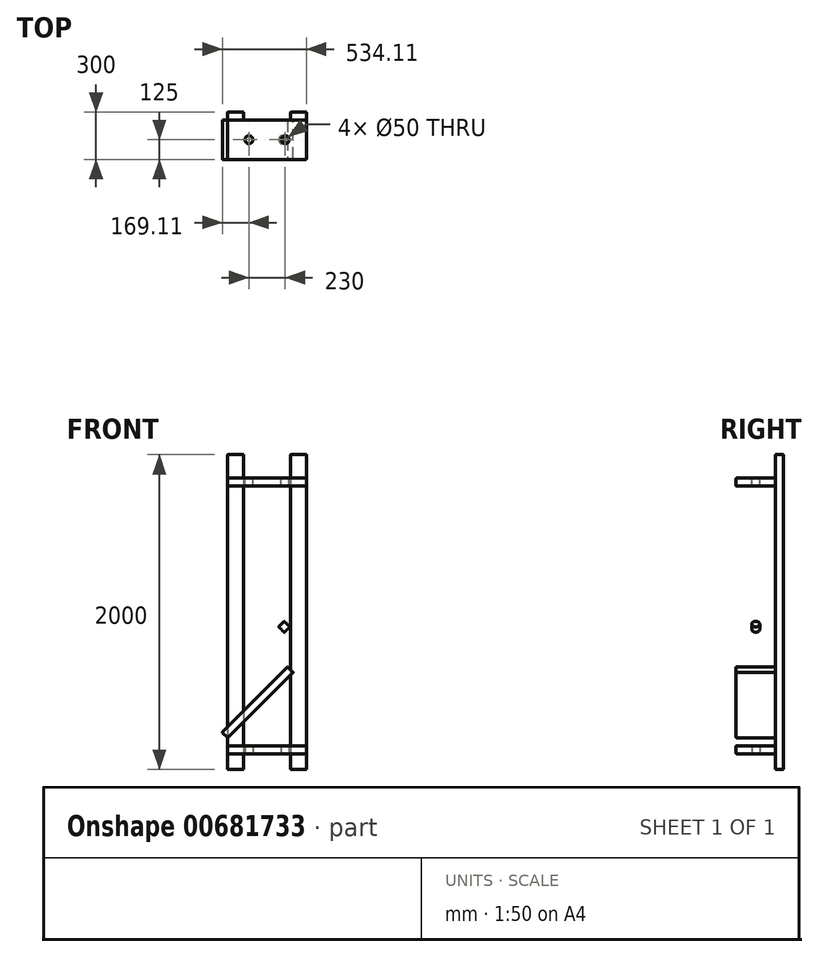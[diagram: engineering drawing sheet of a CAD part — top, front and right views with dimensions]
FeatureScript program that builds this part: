
annotation { "Feature Type Name" : "Feature", "Feature Type Description" : "" }
export const myFeature = defineFeature(function(context is Context, id is Id, definition is map)
    precondition{}
    {
        {
            var Q0;
            Q0=qCreatedBy(makeId("Top.planeOp"),FACE);
            var sketch = newSketch(context, id + "F0", { "sketchPlane" : qUnion([Q0])});
            skLineSegment(sketch, "E0", {"start": v(0, -23.34) * mm, "end": v(0, 25.87) * mm, "construction": true});
            skLineSegment(sketch, "E1.bottom", {"start": v(-250, 50) * mm, "end": v(-150, 50) * mm});
            skLineSegment(sketch, "E1.top", {"start": v(-250, 0) * mm, "end": v(-150, 0) * mm});
            skLineSegment(sketch, "E1.left", {"start": v(-250, 50) * mm, "end": v(-250, 0) * mm});
            skLineSegment(sketch, "E1.right", {"start": v(-150, 50) * mm, "end": v(-150, 0) * mm});
            skLineSegment(sketch, "E2.MirrorCS", {"start": v(150, 50) * mm, "end": v(150, 0) * mm});
            skLineSegment(sketch, "E3.MirrorCS", {"start": v(250, 50) * mm, "end": v(250, 0) * mm});
            skLineSegment(sketch, "E4.MirrorCS", {"start": v(250, 0) * mm, "end": v(150, 0) * mm});
            skLineSegment(sketch, "E5.MirrorCS", {"start": v(250, 50) * mm, "end": v(150, 50) * mm});
            skSolve(sketch);
        }
        {
            var Q0;
            Q0 = qSketchRegion(id + "F0", true);
            extrude(context, id + "F1", {"entities" : qUnion([Q0]), "depth" : 2000 * mm, "offsetDistance" : 25 * mm});
        }
        {
            var Q0;
            Q0=makeQuery(id+"F1.opExtrude","SWEPT_FACE",FACE,{"disambiguationData":[OSD([sQuery(id+"F0.wireOp",EDGE,"E1.top")])]});
            var sketch = newSketch(context, id + "F2", { "sketchPlane" : qUnion([Q0])});
            skLineSegment(sketch, "E6.bottom", {"start": v(-250, 1850) * mm, "end": v(250, 1850) * mm});
            skLineSegment(sketch, "E6.top", {"start": v(-250, 1800) * mm, "end": v(250, 1800) * mm});
            skLineSegment(sketch, "E6.left", {"start": v(-250, 1850) * mm, "end": v(-250, 1800) * mm});
            skLineSegment(sketch, "E6.right", {"start": v(250, 1850) * mm, "end": v(250, 1800) * mm});
            skLineSegment(sketch, "E7.bottom", {"start": v(-250, 150) * mm, "end": v(250, 150) * mm});
            skLineSegment(sketch, "E7.top", {"start": v(-250, 100) * mm, "end": v(250, 100) * mm});
            skLineSegment(sketch, "E7.left", {"start": v(-250, 150) * mm, "end": v(-250, 100) * mm});
            skLineSegment(sketch, "E7.right", {"start": v(250, 150) * mm, "end": v(250, 100) * mm});
            skLineSegment(sketch, "E8", {"start": v(300, 750) * mm, "end": v(-250, 1300) * mm});
            skLineSegment(sketch, "E9.MirrorCS", {"start": v(300, 750) * mm, "end": v(-250, 200) * mm});
            skLineSegment(sketch, "E10", {"start": v(-250, 1300) * mm, "end": v(-285.36, 1264.64) * mm});
            skLineSegment(sketch, "E11", {"start": v(-250, 200) * mm, "end": v(-285.36, 235.36) * mm});
            skLineSegment(sketch, "E12", {"start": v(-285.36, 1264.64) * mm, "end": v(229.29, 750) * mm});
            skLineSegment(sketch, "E13", {"start": v(229.29, 750) * mm, "end": v(-285.36, 235.36) * mm});
            skSolve(sketch);
        }
        {
            var Q0;
            Q0 = qSketchRegion(id + "F2", true);
            extrude(context, id + "F3", {"entities" : qUnion([Q0]), "depth" : 250 * mm, "offsetDistance" : 25 * mm});
        }
        {
            var Q0;
            Q0=makeQuery(id+"F3.opExtrude","SWEPT_FACE",FACE,{"disambiguationData":[OSD([sQuery(id+"F2.wireOp",EDGE,"E6.bottom")])]});
            var sketch = newSketch(context, id + "F4", { "sketchPlane" : qUnion([Q0])});
            skCircle(sketch, "E14", {"center": v(-115, -125) * mm, "radius": 25 * mm});
            skLineSegment(sketch, "E15", {"start": v(0, 0) * mm, "end": v(0, -300.8) * mm, "construction": true});
            skCircle(sketch, "E16.MirrorC", {"center": v(115, -125) * mm, "radius": 25 * mm});
            skSolve(sketch);
        }
        {
            var Q0;
            Q0 = qSketchRegion(id + "F4", true);
            extrude(context, id + "F5", {"entities" : qUnion([Q0]), "operationType" : NewBodyOperationType.REMOVE, "oppositeDirection" : true, "depth" : 128 * mm, "offsetDistance" : 25 * mm});
        }
        {
            var Q0;
            Q0=makeQuery(id+"F3.opExtrude","SWEPT_FACE",FACE,{"disambiguationData":[OSD([sQuery(id+"F2.wireOp",EDGE,"E7.top")])]});
            var sketch = newSketch(context, id + "F6", { "sketchPlane" : qUnion([Q0])});
            skCircle(sketch, "E17", {"center": v(-115, 125) * mm, "radius": 25 * mm});
            skLineSegment(sketch, "E18", {"start": v(0, 0) * mm, "end": v(0, 311.11) * mm, "construction": true});
            skPoint(sketch, "E18.endSnap0", {"position": v(0, 250) * mm});
            skCircle(sketch, "E19.MirrorC", {"center": v(115, 125) * mm, "radius": 25 * mm});
            skSolve(sketch);
        }
        {
            var Q0;
            Q0 = qSketchRegion(id + "F6", true);
            extrude(context, id + "F7", {"entities" : qUnion([Q0]), "operationType" : NewBodyOperationType.REMOVE, "oppositeDirection" : true, "depth" : 94 * mm, "offsetDistance" : 25 * mm});
        }
        {
            var Q0;
            Q0=makeQuery(id+"F3.opExtrude","SWEPT_FACE",FACE,{"disambiguationData":[OSD([sQuery(id+"F2.wireOp",EDGE,"E8")])]});
            var sketch = newSketch(context, id + "F8", { "sketchPlane" : qUnion([Q0])});
            skLineSegment(sketch, "E20", {"start": v(-250, 707.1) * mm, "end": v(0, 707.1) * mm, "construction": true});
            skCircle(sketch, "E21", {"center": v(-125, 851.02) * mm, "radius": 25 * mm});
            skCircle(sketch, "E22.MirrorC", {"center": v(-125, 563.2) * mm, "radius": 25 * mm});
            skSolve(sketch);
        }
        {
            var Q0;
            Q0=makeQuery(id+"F8.imprint","IMPRINT",FACE,{"disambiguationData":[TD([[makeQuery(id+"F8.imprint","IMPRINT",EDGE,{"derivedFrom":sQuery(id+"F8.wireOp",EDGE,"E21")}),1.0]])]});
            var Q1;
            Q1=makeQuery(id+"F8.imprint","IMPRINT",FACE,{"disambiguationData":[TD([[makeQuery(id+"F8.imprint","IMPRINT",EDGE,{"derivedFrom":sQuery(id+"F8.wireOp",EDGE,"E22.MirrorC")}),-1.0]])]});
            extrude(context, id + "F9", {"entities" : qUnion([Q0, Q1]), "operationType" : NewBodyOperationType.REMOVE, "oppositeDirection" : true, "depth" : 190 * mm, "offsetDistance" : 25 * mm});
        }
        {
            var Q0;
            Q0=makeQuery(id+"F3.opExtrude","SWEPT_FACE",FACE,{"disambiguationData":[OSD([sQuery(id+"F2.wireOp",EDGE,"E9.MirrorCS")])]});
            var sketch = newSketch(context, id + "F10", { "sketchPlane" : qUnion([Q0])});
            skCircle(sketch, "E23", {"center": v(497.46, 125) * mm, "radius": 25 * mm});
            skLineSegment(sketch, "E24", {"start": v(353.55, 0) * mm, "end": v(353.55, 250) * mm, "construction": true});
            skCircle(sketch, "E25.MirrorC", {"center": v(209.64, 125) * mm, "radius": 25 * mm});
            skSolve(sketch);
        }
        {
            var Q0;
            Q0 = qSketchRegion(id + "F10", true);
            extrude(context, id + "F11", {"entities" : qUnion([Q0]), "operationType" : NewBodyOperationType.REMOVE, "oppositeDirection" : true, "depth" : 154 * mm, "offsetDistance" : 25 * mm});
        }
        {
            var Q0;
            Q0=makeQuery(id+"F1.opExtrude","SWEPT_EDGE",EDGE,{"disambiguationData":[OSD([sQuery(id+"F0.wireOp",EDGE,"E1.top"),sQuery(id+"F0.wireOp",EDGE,"E1.left")])]});
            var Q1;
            Q1=makeQuery(id+"F1.opExtrude","SWEPT_EDGE",EDGE,{"disambiguationData":[OSD([sQuery(id+"F0.wireOp",EDGE,"E1.top"),sQuery(id+"F0.wireOp",EDGE,"E1.right")])]});
            var Q2;
            Q2=makeQuery(id+"F1.opExtrude","SWEPT_EDGE",EDGE,{"disambiguationData":[OSD([sQuery(id+"F0.wireOp",EDGE,"E3.MirrorCS"),sQuery(id+"F0.wireOp",EDGE,"E4.MirrorCS")])]});
            var Q3;
            Q3=makeQuery(id+"F1.opExtrude","SWEPT_EDGE",EDGE,{"disambiguationData":[OSD([sQuery(id+"F0.wireOp",EDGE,"E2.MirrorCS"),sQuery(id+"F0.wireOp",EDGE,"E4.MirrorCS")])]});
            var Q4;
            Q4=makeQuery(id+"F1.opExtrude","SWEPT_EDGE",EDGE,{"disambiguationData":[OSD([sQuery(id+"F0.wireOp",EDGE,"E3.MirrorCS"),sQuery(id+"F0.wireOp",EDGE,"E5.MirrorCS")])]});
            var Q5;
            Q5=makeQuery(id+"F5.boolean.opBoolean","COPY",EDGE,{"derivedFrom":makeQuery(id+"F5.opExtrude","CAP_EDGE",EDGE,{"disambiguationData":[OSD([sQuery(id+"F4.wireOp",EDGE,"E16.MirrorC")])],"isStart":true})});
            var Q6;
            Q6=makeQuery(id+"F5.boolean.opBoolean","COPY",EDGE,{"derivedFrom":makeQuery(id+"F5.opExtrude","CAP_EDGE",EDGE,{"disambiguationData":[OSD([sQuery(id+"F4.wireOp",EDGE,"E14")])],"isStart":true})});
            var Q7;
            Q7=makeQuery(id+"F3.opExtrude","SWEPT_EDGE",EDGE,{"disambiguationData":[OSD([sQuery(id+"F2.wireOp",EDGE,"E6.top"),sQuery(id+"F2.wireOp",EDGE,"E6.right")])]});
            var Q8;
            Q8=makeQuery(id+"F3.opExtrude","SWEPT_EDGE",EDGE,{"disambiguationData":[OSD([sQuery(id+"F2.wireOp",EDGE,"E6.bottom"),sQuery(id+"F2.wireOp",EDGE,"E6.right")])]});
            var Q9;
            Q9=makeQuery(id+"F3.opExtrude","SWEPT_EDGE",EDGE,{"disambiguationData":[OSD([sQuery(id+"F0.wireOp",EDGE,"E1.top"),sQuery(id+"F0.wireOp",EDGE,"E1.left"),sQuery(id+"F2.wireOp",EDGE,"E6.bottom"),sQuery(id+"F2.wireOp",EDGE,"E6.left")])]});
            var Q10;
            Q10=makeQuery(id+"F3.opExtrude","CAP_EDGE",EDGE,{"disambiguationData":[OSD([sQuery(id+"F2.wireOp",EDGE,"E6.top")])],"isStart":false});
            var Q11;
            Q11=makeQuery(id+"F3.opExtrude","CAP_EDGE",EDGE,{"disambiguationData":[OSD([sQuery(id+"F2.wireOp",EDGE,"E6.bottom")])],"isStart":false});
            var Q12;
            Q12=makeQuery(id+"F3.opExtrude","CAP_EDGE",EDGE,{"disambiguationData":[OSD([sQuery(id+"F2.wireOp",EDGE,"E6.bottom")])],"isStart":true});
            var Q13;
            Q13=makeQuery(id+"F3.opExtrude","SWEPT_EDGE",EDGE,{"disambiguationData":[OSD([sQuery(id+"F0.wireOp",EDGE,"E1.top"),sQuery(id+"F0.wireOp",EDGE,"E1.left"),sQuery(id+"F2.wireOp",EDGE,"E7.bottom"),sQuery(id+"F2.wireOp",EDGE,"E7.left")])]});
            var Q14;
            Q14=makeQuery(id+"F3.opExtrude","SWEPT_EDGE",EDGE,{"disambiguationData":[OSD([sQuery(id+"F0.wireOp",EDGE,"E1.top"),sQuery(id+"F0.wireOp",EDGE,"E1.left"),sQuery(id+"F2.wireOp",EDGE,"E8"),sQuery(id+"F2.wireOp",EDGE,"E10")])]});
            var Q15;
            Q15=makeQuery(id+"F3.opExtrude","SWEPT_EDGE",EDGE,{"disambiguationData":[OSD([sQuery(id+"F2.wireOp",EDGE,"E8"),sQuery(id+"F2.wireOp",EDGE,"E9.MirrorCS")])]});
            var Q16;
            Q16=makeQuery(id+"F11.boolean.opBoolean","INTERSECT",EDGE,{"derivedFrom":[makeQuery(id+"F3.opExtrude","SWEPT_FACE",FACE,{"disambiguationData":[OSD([sQuery(id+"F2.wireOp",EDGE,"E13")])]}),makeQuery(id+"F11.opExtrude","SWEPT_FACE",FACE,{"disambiguationData":[OSD([sQuery(id+"F10.wireOp",EDGE,"E25.MirrorC")])]})]});
            var Q17;
            Q17=makeQuery(id+"F3.opExtrude","SWEPT_EDGE",EDGE,{"disambiguationData":[OSD([sQuery(id+"F2.wireOp",EDGE,"E11"),sQuery(id+"F2.wireOp",EDGE,"E13")])]});
            var Q18;
            Q18=makeQuery(id+"F3.opExtrude","CAP_EDGE",EDGE,{"disambiguationData":[OSD([sQuery(id+"F2.wireOp",EDGE,"E9.MirrorCS")])],"isStart":false});
            var Q19;
            Q19=makeQuery(id+"F3.opExtrude","CAP_EDGE",EDGE,{"disambiguationData":[OSD([sQuery(id+"F2.wireOp",EDGE,"E13")])],"isStart":false});
            var Q20;
            Q20=makeQuery(id+"F3.opExtrude","CAP_EDGE",EDGE,{"disambiguationData":[OSD([sQuery(id+"F2.wireOp",EDGE,"E12")])],"isStart":false});
            var Q21;
            Q21=makeQuery(id+"F3.opExtrude","CAP_EDGE",EDGE,{"disambiguationData":[OSD([sQuery(id+"F2.wireOp",EDGE,"E8")])],"isStart":false});
            var Q22;
            Q22=makeQuery(id+"F3.opExtrude","CAP_EDGE",EDGE,{"disambiguationData":[OSD([sQuery(id+"F2.wireOp",EDGE,"E13")])],"isStart":true});
            var Q23;
            Q23=makeQuery(id+"F3.opExtrude","CAP_EDGE",EDGE,{"disambiguationData":[OSD([sQuery(id+"F2.wireOp",EDGE,"E8")])],"isStart":true});
            var Q24;
            Q24=makeQuery(id+"F9.boolean.opBoolean","COPY",EDGE,{"derivedFrom":makeQuery(id+"F9.opExtrude","CAP_EDGE",EDGE,{"disambiguationData":[OSD([sQuery(id+"F8.wireOp",EDGE,"E21")])],"isStart":true})});
            var Q25;
            Q25=makeQuery(id+"F9.boolean.opBoolean","COPY",EDGE,{"derivedFrom":makeQuery(id+"F9.opExtrude","CAP_EDGE",EDGE,{"disambiguationData":[OSD([sQuery(id+"F8.wireOp",EDGE,"E22.MirrorC")])],"isStart":true})});
            var Q26;
            Q26=makeQuery(id+"F1.opExtrude","SWEPT_EDGE",EDGE,{"disambiguationData":[OSD([sQuery(id+"F0.wireOp",EDGE,"E1.bottom"),sQuery(id+"F0.wireOp",EDGE,"E1.left")])]});
            var Q27;
            Q27=makeQuery(id+"F1.opExtrude","SWEPT_EDGE",EDGE,{"disambiguationData":[OSD([sQuery(id+"F0.wireOp",EDGE,"E1.bottom"),sQuery(id+"F0.wireOp",EDGE,"E1.right")])]});
            var Q28;
            Q28=makeQuery(id+"F1.opExtrude","CAP_EDGE",EDGE,{"disambiguationData":[OSD([sQuery(id+"F0.wireOp",EDGE,"E1.right")])],"isStart":false});
            var Q29;
            Q29=makeQuery(id+"F1.opExtrude","CAP_EDGE",EDGE,{"disambiguationData":[OSD([sQuery(id+"F0.wireOp",EDGE,"E1.top")])],"isStart":false});
            var Q30;
            Q30=makeQuery(id+"F1.opExtrude","SWEPT_EDGE",EDGE,{"disambiguationData":[OSD([sQuery(id+"F0.wireOp",EDGE,"E2.MirrorCS"),sQuery(id+"F0.wireOp",EDGE,"E5.MirrorCS")])]});
            var Q31;
            Q31=makeQuery(id+"F1.opExtrude","CAP_EDGE",EDGE,{"disambiguationData":[OSD([sQuery(id+"F0.wireOp",EDGE,"E4.MirrorCS")])],"isStart":false});
            var Q32;
            Q32=makeQuery(id+"F1.opExtrude","CAP_EDGE",EDGE,{"disambiguationData":[OSD([sQuery(id+"F0.wireOp",EDGE,"E4.MirrorCS")])],"isStart":true});
            var Q33;
            Q33=makeQuery(id+"F3.opExtrude","SWEPT_EDGE",EDGE,{"disambiguationData":[OSD([sQuery(id+"F0.wireOp",EDGE,"E1.top"),sQuery(id+"F0.wireOp",EDGE,"E1.left"),sQuery(id+"F2.wireOp",EDGE,"E6.top"),sQuery(id+"F2.wireOp",EDGE,"E6.left")])]});
            var Q34;
            Q34=makeQuery(id+"F5.boolean.opBoolean","INTERSECT",EDGE,{"derivedFrom":[makeQuery(id+"F3.opExtrude","SWEPT_FACE",FACE,{"disambiguationData":[OSD([sQuery(id+"F2.wireOp",EDGE,"E6.top")])]}),makeQuery(id+"F5.opExtrude","SWEPT_FACE",FACE,{"disambiguationData":[OSD([sQuery(id+"F4.wireOp",EDGE,"E16.MirrorC")])]})]});
            var Q35;
            Q35=makeQuery(id+"F3.opExtrude","CAP_EDGE",EDGE,{"disambiguationData":[OSD([sQuery(id+"F2.wireOp",EDGE,"E6.right")])],"isStart":false});
            var Q36;
            Q36=makeQuery(id+"F3.opExtrude","CAP_EDGE",EDGE,{"disambiguationData":[OSD([sQuery(id+"F2.wireOp",EDGE,"E6.left")])],"isStart":false});
            var Q37;
            Q37=makeQuery(id+"F3.opExtrude","CAP_EDGE",EDGE,{"disambiguationData":[OSD([sQuery(id+"F2.wireOp",EDGE,"E6.top")])],"isStart":true});
            var Q38;
            Q38=makeQuery(id+"F3.opExtrude","CAP_EDGE",EDGE,{"disambiguationData":[OSD([sQuery(id+"F2.wireOp",EDGE,"E6.right")])],"isStart":true});
            var Q39;
            Q39=makeQuery(id+"F3.opExtrude","CAP_EDGE",EDGE,{"disambiguationData":[OSD([sQuery(id+"F2.wireOp",EDGE,"E6.left")])],"isStart":true});
            var Q40;
            Q40=makeQuery(id+"F7.boolean.opBoolean","COPY",EDGE,{"derivedFrom":makeQuery(id+"F7.opExtrude","CAP_EDGE",EDGE,{"disambiguationData":[OSD([sQuery(id+"F6.wireOp",EDGE,"E17")])],"isStart":true})});
            var Q41;
            Q41=makeQuery(id+"F3.opExtrude","CAP_EDGE",EDGE,{"disambiguationData":[OSD([sQuery(id+"F2.wireOp",EDGE,"E7.left")])],"isStart":false});
            var Q42;
            Q42=makeQuery(id+"F3.opExtrude","CAP_EDGE",EDGE,{"disambiguationData":[OSD([sQuery(id+"F2.wireOp",EDGE,"E7.bottom")])],"isStart":false});
            var Q43;
            Q43=makeQuery(id+"F7.boolean.opBoolean","INTERSECT",EDGE,{"derivedFrom":[makeQuery(id+"F3.opExtrude","SWEPT_FACE",FACE,{"disambiguationData":[OSD([sQuery(id+"F2.wireOp",EDGE,"E7.bottom")])]}),makeQuery(id+"F7.opExtrude","SWEPT_FACE",FACE,{"disambiguationData":[OSD([sQuery(id+"F6.wireOp",EDGE,"E17")])]})]});
            var Q44;
            Q44=makeQuery(id+"F3.opExtrude","CAP_EDGE",EDGE,{"disambiguationData":[OSD([sQuery(id+"F2.wireOp",EDGE,"E7.top")])],"isStart":true});
            var Q45;
            Q45=makeQuery(id+"F7.boolean.opBoolean","INTERSECT",EDGE,{"derivedFrom":[makeQuery(id+"F3.opExtrude","SWEPT_FACE",FACE,{"disambiguationData":[OSD([sQuery(id+"F2.wireOp",EDGE,"E7.bottom")])]}),makeQuery(id+"F7.opExtrude","SWEPT_FACE",FACE,{"disambiguationData":[OSD([sQuery(id+"F6.wireOp",EDGE,"E19.MirrorC")])]})]});
            var Q46;
            Q46=makeQuery(id+"F3.opExtrude","CAP_EDGE",EDGE,{"disambiguationData":[OSD([sQuery(id+"F2.wireOp",EDGE,"E7.top")])],"isStart":false});
            var Q47;
            Q47=makeQuery(id+"F3.opExtrude","SWEPT_EDGE",EDGE,{"disambiguationData":[OSD([sQuery(id+"F2.wireOp",EDGE,"E7.top"),sQuery(id+"F2.wireOp",EDGE,"E7.right")])]});
            var Q48;
            Q48=makeQuery(id+"F3.opExtrude","SWEPT_EDGE",EDGE,{"disambiguationData":[OSD([sQuery(id+"F2.wireOp",EDGE,"E7.bottom"),sQuery(id+"F2.wireOp",EDGE,"E7.right")])]});
            var Q49;
            Q49=makeQuery(id+"F3.opExtrude","CAP_EDGE",EDGE,{"disambiguationData":[OSD([sQuery(id+"F2.wireOp",EDGE,"E7.bottom")])],"isStart":true});
            var Q50;
            Q50=makeQuery(id+"F3.opExtrude","SWEPT_EDGE",EDGE,{"disambiguationData":[OSD([sQuery(id+"F0.wireOp",EDGE,"E1.top"),sQuery(id+"F0.wireOp",EDGE,"E1.left"),sQuery(id+"F2.wireOp",EDGE,"E9.MirrorCS"),sQuery(id+"F2.wireOp",EDGE,"E11")])]});
            var Q51;
            Q51=makeQuery(id+"F3.opExtrude","CAP_EDGE",EDGE,{"disambiguationData":[OSD([sQuery(id+"F2.wireOp",EDGE,"E10")])],"isStart":false});
            var Q52;
            Q52=makeQuery(id+"F3.opExtrude","CAP_EDGE",EDGE,{"disambiguationData":[OSD([sQuery(id+"F2.wireOp",EDGE,"E11")])],"isStart":true});
            var Q53;
            Q53=makeQuery(id+"F11.boolean.opBoolean","COPY",EDGE,{"derivedFrom":makeQuery(id+"F11.opExtrude","CAP_EDGE",EDGE,{"disambiguationData":[OSD([sQuery(id+"F10.wireOp",EDGE,"E23")])],"isStart":true})});
            var Q54;
            Q54=makeQuery(id+"F3.opExtrude","CAP_EDGE",EDGE,{"disambiguationData":[OSD([sQuery(id+"F2.wireOp",EDGE,"E11")])],"isStart":false});
            var Q55;
            Q55=makeQuery(id+"F3.opExtrude","SWEPT_EDGE",EDGE,{"disambiguationData":[OSD([sQuery(id+"F2.wireOp",EDGE,"E12"),sQuery(id+"F2.wireOp",EDGE,"E13")])]});
            var Q56;
            Q56=makeQuery(id+"F3.opExtrude","CAP_EDGE",EDGE,{"disambiguationData":[OSD([sQuery(id+"F2.wireOp",EDGE,"E10")])],"isStart":true});
            var Q57;
            Q57=makeQuery(id+"F3.opExtrude","CAP_EDGE",EDGE,{"disambiguationData":[OSD([sQuery(id+"F2.wireOp",EDGE,"E12")])],"isStart":true});
            var Q58;
            Q58=makeQuery(id+"F3.opExtrude","CAP_EDGE",EDGE,{"disambiguationData":[OSD([sQuery(id+"F2.wireOp",EDGE,"E9.MirrorCS")])],"isStart":true});
            var Q59;
            Q59=makeQuery(id+"F9.boolean.opBoolean","INTERSECT",EDGE,{"derivedFrom":[makeQuery(id+"F3.opExtrude","SWEPT_FACE",FACE,{"disambiguationData":[OSD([sQuery(id+"F2.wireOp",EDGE,"E12")])]}),makeQuery(id+"F9.opExtrude","SWEPT_FACE",FACE,{"disambiguationData":[OSD([sQuery(id+"F8.wireOp",EDGE,"E22.MirrorC")])]})]});
            var Q60;
            Q60=makeQuery(id+"F11.boolean.opBoolean","INTERSECT",EDGE,{"derivedFrom":[makeQuery(id+"F3.opExtrude","SWEPT_FACE",FACE,{"disambiguationData":[OSD([sQuery(id+"F2.wireOp",EDGE,"E13")])]}),makeQuery(id+"F11.opExtrude","SWEPT_FACE",FACE,{"disambiguationData":[OSD([sQuery(id+"F10.wireOp",EDGE,"E23")])]})]});
            var Q61;
            Q61=makeQuery(id+"F1.opExtrude","CAP_EDGE",EDGE,{"disambiguationData":[OSD([sQuery(id+"F0.wireOp",EDGE,"E1.bottom")])],"isStart":false});
            var Q62;
            Q62=makeQuery(id+"F1.opExtrude","CAP_EDGE",EDGE,{"disambiguationData":[OSD([sQuery(id+"F0.wireOp",EDGE,"E1.left")])],"isStart":false});
            var Q63;
            Q63=makeQuery(id+"F1.opExtrude","CAP_EDGE",EDGE,{"disambiguationData":[OSD([sQuery(id+"F0.wireOp",EDGE,"E2.MirrorCS")])],"isStart":false});
            var Q64;
            Q64=makeQuery(id+"F1.opExtrude","CAP_EDGE",EDGE,{"disambiguationData":[OSD([sQuery(id+"F0.wireOp",EDGE,"E5.MirrorCS")])],"isStart":false});
            var Q65;
            Q65=makeQuery(id+"F1.opExtrude","CAP_EDGE",EDGE,{"disambiguationData":[OSD([sQuery(id+"F0.wireOp",EDGE,"E3.MirrorCS")])],"isStart":false});
            var Q66;
            Q66=makeQuery(id+"F1.opExtrude","CAP_EDGE",EDGE,{"disambiguationData":[OSD([sQuery(id+"F0.wireOp",EDGE,"E5.MirrorCS")])],"isStart":true});
            var Q67;
            Q67=makeQuery(id+"F1.opExtrude","CAP_EDGE",EDGE,{"disambiguationData":[OSD([sQuery(id+"F0.wireOp",EDGE,"E3.MirrorCS")])],"isStart":true});
            var Q68;
            Q68=makeQuery(id+"F5.boolean.opBoolean","INTERSECT",EDGE,{"derivedFrom":[makeQuery(id+"F3.opExtrude","SWEPT_FACE",FACE,{"disambiguationData":[OSD([sQuery(id+"F2.wireOp",EDGE,"E6.top")])]}),makeQuery(id+"F5.opExtrude","SWEPT_FACE",FACE,{"disambiguationData":[OSD([sQuery(id+"F4.wireOp",EDGE,"E14")])]})]});
            var Q69;
            Q69=makeQuery(id+"F7.boolean.opBoolean","COPY",EDGE,{"derivedFrom":makeQuery(id+"F7.opExtrude","CAP_EDGE",EDGE,{"disambiguationData":[OSD([sQuery(id+"F6.wireOp",EDGE,"E19.MirrorC")])],"isStart":true})});
            var Q70;
            Q70=makeQuery(id+"F3.opExtrude","SWEPT_EDGE",EDGE,{"disambiguationData":[OSD([sQuery(id+"F0.wireOp",EDGE,"E1.top"),sQuery(id+"F0.wireOp",EDGE,"E1.left"),sQuery(id+"F2.wireOp",EDGE,"E7.top"),sQuery(id+"F2.wireOp",EDGE,"E7.left")])]});
            var Q71;
            Q71=makeQuery(id+"F3.opExtrude","CAP_EDGE",EDGE,{"disambiguationData":[OSD([sQuery(id+"F2.wireOp",EDGE,"E7.right")])],"isStart":false});
            var Q72;
            Q72=makeQuery(id+"F3.opExtrude","CAP_EDGE",EDGE,{"disambiguationData":[OSD([sQuery(id+"F2.wireOp",EDGE,"E7.left")])],"isStart":true});
            var Q73;
            Q73=makeQuery(id+"F3.opExtrude","CAP_EDGE",EDGE,{"disambiguationData":[OSD([sQuery(id+"F2.wireOp",EDGE,"E7.right")])],"isStart":true});
            var Q74;
            Q74=makeQuery(id+"F3.opExtrude","SWEPT_EDGE",EDGE,{"disambiguationData":[OSD([sQuery(id+"F2.wireOp",EDGE,"E10"),sQuery(id+"F2.wireOp",EDGE,"E12")])]});
            var Q75;
            Q75=makeQuery(id+"F9.boolean.opBoolean","INTERSECT",EDGE,{"derivedFrom":[makeQuery(id+"F3.opExtrude","SWEPT_FACE",FACE,{"disambiguationData":[OSD([sQuery(id+"F2.wireOp",EDGE,"E12")])]}),makeQuery(id+"F9.opExtrude","SWEPT_FACE",FACE,{"disambiguationData":[OSD([sQuery(id+"F8.wireOp",EDGE,"E21")])]})]});
            var Q76;
            Q76=makeQuery(id+"F11.boolean.opBoolean","COPY",EDGE,{"derivedFrom":makeQuery(id+"F11.opExtrude","CAP_EDGE",EDGE,{"disambiguationData":[OSD([sQuery(id+"F10.wireOp",EDGE,"E25.MirrorC")])],"isStart":true})});
            var Q77;
            Q77=makeQuery(id+"F1.opExtrude","CAP_EDGE",EDGE,{"disambiguationData":[OSD([sQuery(id+"F0.wireOp",EDGE,"E1.right")])],"isStart":true});
            var Q78;
            Q78=makeQuery(id+"F1.opExtrude","CAP_EDGE",EDGE,{"disambiguationData":[OSD([sQuery(id+"F0.wireOp",EDGE,"E1.top")])],"isStart":true});
            var Q79;
            Q79=makeQuery(id+"F1.opExtrude","CAP_EDGE",EDGE,{"disambiguationData":[OSD([sQuery(id+"F0.wireOp",EDGE,"E2.MirrorCS")])],"isStart":true});
            var Q80;
            Q80=makeQuery(id+"F1.opExtrude","CAP_EDGE",EDGE,{"disambiguationData":[OSD([sQuery(id+"F0.wireOp",EDGE,"E1.bottom")])],"isStart":true});
            var Q81;
            Q81=makeQuery(id+"F1.opExtrude","CAP_EDGE",EDGE,{"disambiguationData":[OSD([sQuery(id+"F0.wireOp",EDGE,"E1.left")])],"isStart":true});
            fillet(context, id + "F12", {"entities" : qUnion([Q0, Q1, Q2, Q3, Q4, Q5, Q6, Q7, Q8, Q9, Q10, Q11, Q12, Q13, Q14, Q15, Q16, Q17, Q18, Q19, Q20, Q21, Q22, Q23, Q24, Q25, Q26, Q27, Q28, Q29, Q30, Q31, Q32, Q33, Q34, Q35, Q36, Q37, Q38, Q39, Q40, Q41, Q42, Q43, Q44, Q45, Q46, Q47, Q48, Q49, Q50, Q51, Q52, Q53, Q54, Q55, Q56, Q57, Q58, Q59, Q60, Q61, Q62, Q63, Q64, Q65, Q66, Q67, Q68, Q69, Q70, Q71, Q72, Q73, Q74, Q75, Q76, Q77, Q78, Q79, Q80, Q81]), "radius" : 3 * mm, "tangentPropagation" : true, "allowEdgeOverflow" : false});
        }
    });
